# Revit family: Sanitary_Taps-Mixers_AXOR_36723XXX-AXOR-ShowerSolutions-Thermostat222
name_source: partatom
category: Plumbing Fixtures
revit_build: Autodesk Revit 2018 (Build: 20170223_1515(x64)
units: mm (PartAtom-declared; Revit-internal decimal feet)

## family parameters
Always vertical = No
Cut with Voids When Loaded = No
OmniClass Number = 23.27.31.29.15
OmniClass Title = Thermostatically Controlled Mixing Valves
Part Type = Normal
Room Calculation Point = No
Round Connector Dimension = Use Diameter
Shared = No
Work Plane-Based = Yes

## types (1)
- Default - please load Revit Family Type Catalog
    Always visible = Yes
    BIMobject category = Taps & Mixers
    Default Elevation = 1219.2 mm
    Description = AXOR ShowerSolutions Thermostat for concealed installation round for 2 functions
    Design country = Germany
    EAN code = 4011097779348
    Edition number = 1
    GTIN code = https://4011097779348
    IFC Classification = Valve
    Installation instructions = https://www.axor-design.com
    Manufacturer = AXOR
    Manufacturer country = Germany
    Manufacturer name = AXOR
    Material 1 = AXOR - Plastic - Dark Gray
    Material 2 = AXOR - Metal - 000 Chrome
    Model = 36723XXX
    OmniClass Code = 23-27 31 29 15
    OmniClass Description = Thermostatically Controlled Mixing Valves
    Product Guid = 5e18dc03-b91e-41d2-8b04-ec4d862f1efb
    Product SKU = 36723XXX
    Product data url = https://www.bimobject.com
    Product family = AXOR ShowerSolutions
    Product group = Shower thermostat
    Product name = 36723XXX AXOR ShowerSolutions Thermostat for concealed installation round for 2 functions
    Product url = https://www.axor-design.com
    QR code = https://www.bimobject.com
    URL = https://www.axor-design.com
    Weight Net (Kg) = 2

## geometry (parser evidence)
native form markers: Sweep x2
no freeform markers — native parametric forms only
